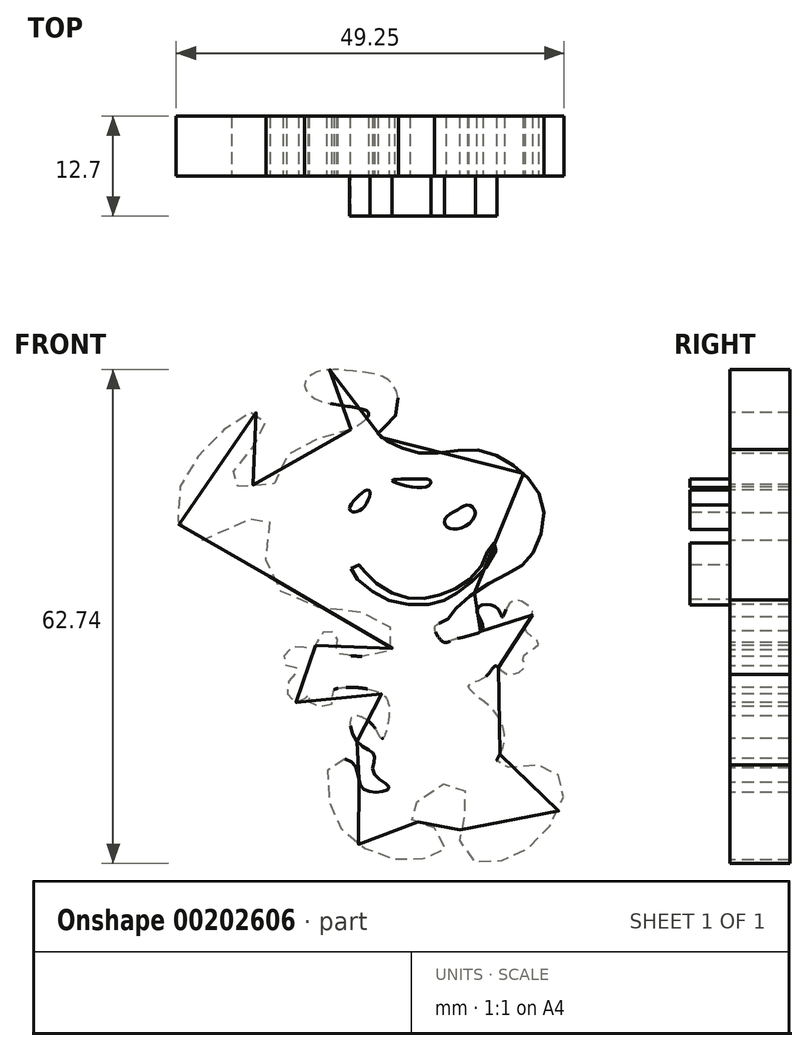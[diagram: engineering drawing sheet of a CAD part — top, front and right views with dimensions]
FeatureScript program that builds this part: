
annotation { "Feature Type Name" : "Feature", "Feature Type Description" : "" }
export const myFeature = defineFeature(function(context is Context, id is Id, definition is map)
    precondition{}
    {
        {
            var Q0;
            Q0=qCreatedBy(makeId("Front.planeOp"),FACE);
            var sketch = newSketch(context, id + "F0", { "sketchPlane" : qUnion([Q0])});
            skFitSpline(sketch, "E0", {"points": [v(-75.27, 12.46) * mm, v(-80.73, 10.85) * mm, v(-84.32, 7.75) * mm, v(-85.44, 4.77) * mm, v(-86.68, 5.4) * mm, v(-89.4, 5.15) * mm, v(-90.4, 5.77) * mm, v(-89.53, 8.25) * mm, v(-86.3, 12.09) * mm, v(-86.43, 14.07) * mm, v(-88.04, 14.57) * mm, v(-91.88, 11.96) * mm, v(-95.97, 7.25) * mm, v(-97.46, 2.17) * mm, v(-94.86, -1.67) * mm, v(-85.93, 1.8) * mm, v(-86.06, -1.8) * mm, v(-84.82, -7.5) * mm, v(-77.87, -10.35) * mm, v(-71.18, -11.71) * mm, v(-69.82, -14.94) * mm, v(-71.92, -16.3) * mm, v(-76.26, -16.18) * mm, v(-77.13, -15.68) * mm, v(-77.13, -13.57) * mm, v(-79.11, -13.57) * mm, v(-80.1, -15.56) * mm, v(-82.46, -15.06) * mm, v(-83.82, -17.3) * mm, v(-81.96, -17.91) * mm, v(-83.45, -20.14) * mm, v(-81.96, -22.25) * mm, v(-80.6, -21.13) * mm, v(-80.6, -22.25) * mm, v(-77.5, -22.25) * mm, v(-77.75, -20.89) * mm, v(-71.92, -20.89) * mm, v(-70.44, -23.61) * mm, v(-71.3, -26.84) * mm, v(-72.54, -25.1) * mm, v(-75.15, -24.1) * mm, v(-74.4, -27.33) * mm, v(-72.3, -28.94) * mm, v(-72.42, -31.18) * mm, v(-70.44, -33.03) * mm, v(-72.05, -33.65) * mm, v(-74.03, -32.79) * mm, v(-74.9, -30.06) * mm, v(-77.63, -29.69) * mm, v(-78.12, -34.4) * mm, v(-76.14, -38.74) * mm, v(-71.06, -41.84) * mm, v(-66.22, -42.08) * mm, v(-63.25, -40.72) * mm, v(-65.23, -37.87) * mm, v(-67.7, -37) * mm, v(-66.35, -34.27) * mm, v(-61.76, -32.54) * mm, v(-60.52, -35.14) * mm, v(-61.51, -38.86) * mm, v(-59.9, -42.33) * mm, v(-55.47, -42.1) * mm, v(-51.46, -39.63) * mm, v(-48.31, -34.38) * mm, v(-48.89, -31.52) * mm, v(-51.56, -30.19) * mm, v(-56.23, -30.47) * mm, v(-56.8, -29.8) * mm, v(-56.04, -28.09) * mm, v(-56.8, -23.7) * mm, v(-60.33, -20.17) * mm, v(-58.14, -18.93) * mm, v(-56.9, -17.6) * mm, v(-55.37, -18.65) * mm, v(-53.27, -17.7) * mm, v(-53.37, -16.36) * mm, v(-51.46, -14.74) * mm, v(-53.18, -13.02) * mm, v(-52.22, -10.92) * mm, v(-54.7, -9.3) * mm, v(-56.04, -11.4) * mm, v(-56.8, -10.16) * mm, v(-59.28, -10.35) * mm, v(-58.52, -12.83) * mm, v(-62.24, -14.26) * mm, v(-63.57, -14.55) * mm, v(-64.62, -12.64) * mm, v(-63.38, -11.97) * mm, v(-61.85, -10.16) * mm, v(-56.13, -6.25) * mm, v(-52.41, -3.68) * mm, v(-50.89, 2.8) * mm, v(-54.03, 7.39) * mm, v(-59.28, 9.86) * mm, v(-65.67, 9.39) * mm, v(-70.25, 10.72) * mm, v(-71.87, 12.06) * mm, v(-69.86, 13.77) * mm, v(-70.06, 18.26) * mm, v(-75.1, 19.88) * mm, v(-79.11, 19.88) * mm, v(-81.12, 18.45) * mm, v(-79.5, 16.16) * mm, v(-73.1, 14.63) * mm, v(-75.27, 12.46) * mm]});
            skFitSpline(sketch, "E1", {"points": [v(-73.01, 4.72) * mm, v(-75.27, 2.9) * mm, v(-75.27, 2.05) * mm, v(-73.68, 2.52) * mm, v(-73.01, 4.72) * mm]});
            skFitSpline(sketch, "E2", {"points": [v(-70.06, 5.96) * mm, v(-67.86, 5.2) * mm, v(-65.29, 5.38) * mm, v(-65.2, 5.96) * mm, v(-66.53, 6.15) * mm, v(-68.43, 6.15) * mm, v(-70.06, 5.96) * mm]});
            skFitSpline(sketch, "E3", {"points": [v(-61.76, 2.24) * mm, v(-63.38, 1) * mm, v(-63, 0) * mm, v(-61.1, 0) * mm, v(-59.47, 1.76) * mm, v(-60.23, 2.8) * mm, v(-61.76, 2.24) * mm]});
            skFitSpline(sketch, "E4", {"points": [v(-75.27, -5.2) * mm, v(-73.49, -7.5) * mm, v(-69.3, -9.59) * mm, v(-64.43, -9.59) * mm, v(-61.85, -8.35) * mm, v(-58.23, -5.2) * mm, v(-56.8, -2.15) * mm, v(-57.47, -2.15) * mm, v(-58.42, -4.44) * mm, v(-61.19, -7.3) * mm, v(-64.52, -8.73) * mm, v(-67.77, -9.02) * mm, v(-71.3, -7.68) * mm, v(-73.77, -5.3) * mm, v(-74.35, -4.73) * mm, v(-75.27, -5.2) * mm]});
            skSolve(sketch);
        }
        {
            var Q0;
            Q0 = qSketchRegion(id + "F0", true);
            var Q1;
            Q1=makeQuery(id+"F0.imprint","IMPRINT",FACE,{"disambiguationData":[TD([[makeQuery(id+"F0.imprint","IMPRINT",EDGE,{"derivedFrom":sQuery(id+"F0.wireOp",EDGE,"E1")}),1.0]])]});
            var Q2;
            Q2=makeQuery(id+"F0.imprint","IMPRINT",FACE,{"disambiguationData":[TD([[makeQuery(id+"F0.imprint","IMPRINT",EDGE,{"derivedFrom":sQuery(id+"F0.wireOp",EDGE,"E2")}),1.0]])]});
            var Q3;
            Q3=makeQuery(id+"F0.imprint","IMPRINT",FACE,{"disambiguationData":[TD([[makeQuery(id+"F0.imprint","IMPRINT",EDGE,{"derivedFrom":sQuery(id+"F0.wireOp",EDGE,"E3")}),1.0]])]});
            var Q4;
            Q4=makeQuery(id+"F0.imprint","IMPRINT",FACE,{"disambiguationData":[TD([[makeQuery(id+"F0.imprint","IMPRINT",EDGE,{"derivedFrom":sQuery(id+"F0.wireOp",EDGE,"E4")}),1.0]])]});
            extrude(context, id + "F1", {"entities" : qUnion([Q0, Q1, Q2, Q3, Q4]), "oppositeDirection" : true, "depth" : 7.62 * mm});
        }
        {
            var Q0;
            Q0=makeQuery(id+"F0.imprint","IMPRINT",FACE,{"disambiguationData":[TD([[makeQuery(id+"F0.imprint","IMPRINT",EDGE,{"derivedFrom":sQuery(id+"F0.wireOp",EDGE,"E1")}),1.0]])]});
            var Q1;
            Q1=makeQuery(id+"F0.imprint","IMPRINT",FACE,{"disambiguationData":[TD([[makeQuery(id+"F0.imprint","IMPRINT",EDGE,{"derivedFrom":sQuery(id+"F0.wireOp",EDGE,"E2")}),1.0]])]});
            var Q2;
            Q2=makeQuery(id+"F0.imprint","IMPRINT",FACE,{"disambiguationData":[TD([[makeQuery(id+"F0.imprint","IMPRINT",EDGE,{"derivedFrom":sQuery(id+"F0.wireOp",EDGE,"E3")}),1.0]])]});
            var Q3;
            Q3=makeQuery(id+"F0.imprint","IMPRINT",FACE,{"disambiguationData":[TD([[makeQuery(id+"F0.imprint","IMPRINT",EDGE,{"derivedFrom":sQuery(id+"F0.wireOp",EDGE,"E4")}),1.0]])]});
            extrude(context, id + "F2", {"entities" : qUnion([Q0, Q1, Q2, Q3]), "operationType" : NewBodyOperationType.ADD, "depth" : 5.08 * mm});
        }
    });
